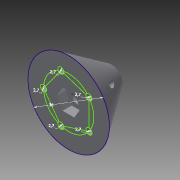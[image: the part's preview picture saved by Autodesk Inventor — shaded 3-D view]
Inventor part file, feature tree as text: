
AUTODESK INVENTOR PART (.ipt)
format: ipt  version: 2014 SP2 (Build 180246200, 246)  size: 151,552 bytes
history: native  units: mm
features: extrude x4, sketch x3, chamfer x1
ambient origin geometry x8: Origin, YZ Plane, XZ Plane, XY Plane, X Axis, Y Axis, Z Axis, Center Point
bodies: Solid1 (feature_tree)
feature tree (8):
  sketch  "Sketch1"  dims[d0=36.0mm d1=22.2mm]
  extrude  "Extrusion1"  Depth=22.2mm
  extrude  "Extrusion3"  Depth=2.7mm
  extrude  "Extrusion4"  Depth=2.7mm
  chamfer  "Chamfer2"  Distance=2.7mm
  extrude  "Extrusion5"  Depth=19.0mm TaperAngle=0.0deg
  sketch  "Sketch3"  dims[d2=2.7mm d3=2.7mm]
  sketch  "Sketch4"  dims[d4=2.7mm d5=2.7mm d6=2.7mm d7=19.0mm d8=0.0mm d23=9.0mm d24=4.0mm d25=0.0mm d26=5.5mm d27=17.0mm d28=0.0mm d32=13.0mm d33=19.0mm d34=45.0deg d40=14.0mm d41=0.0mm]
